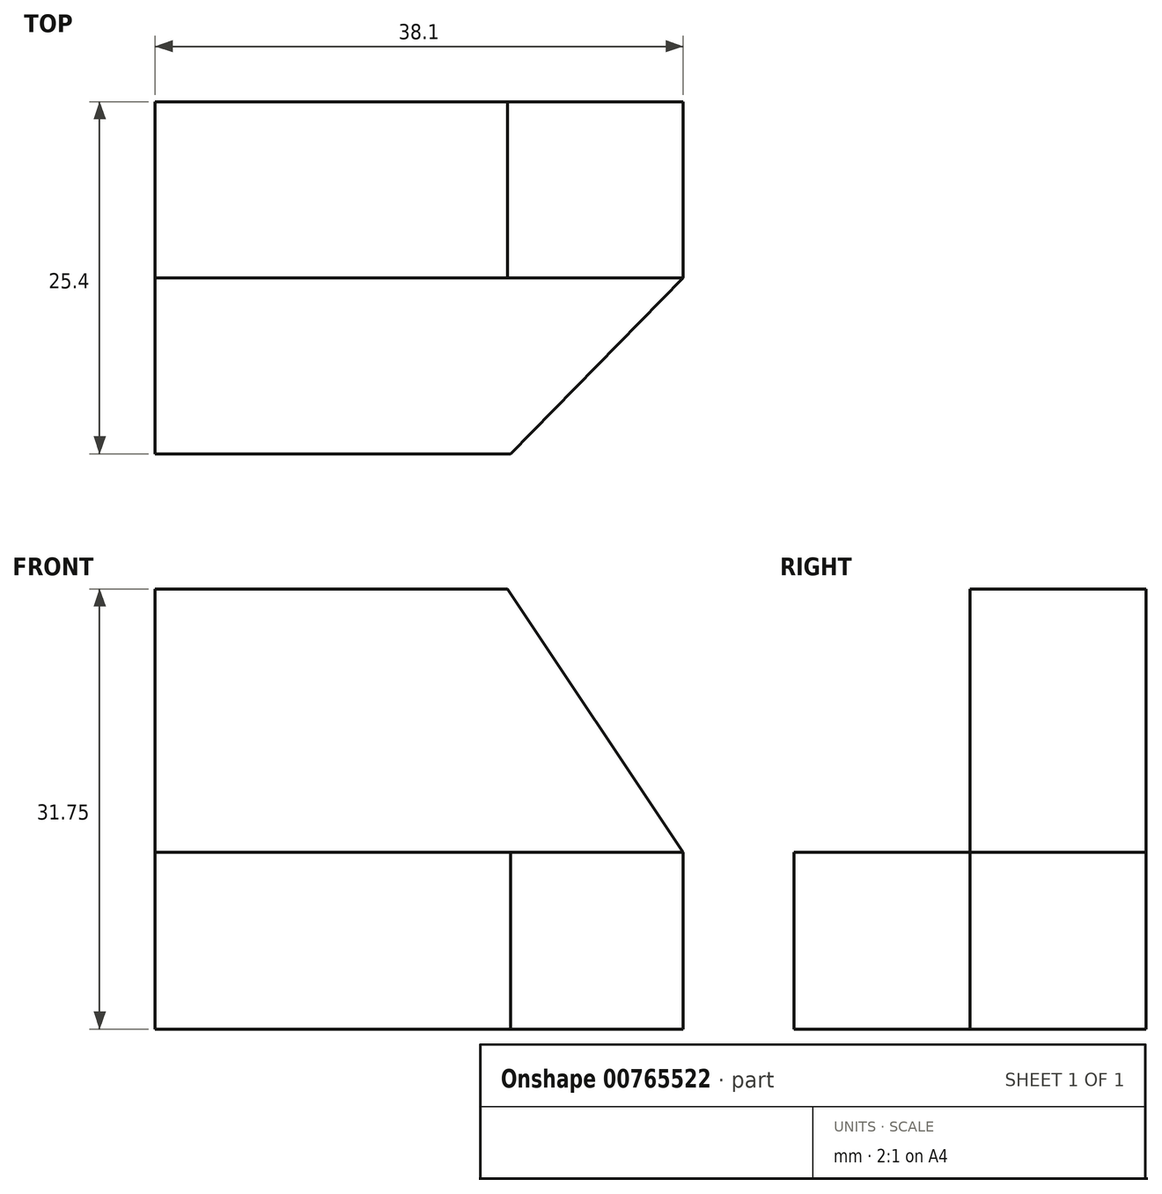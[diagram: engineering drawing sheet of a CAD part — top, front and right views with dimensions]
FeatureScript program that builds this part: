
annotation { "Feature Type Name" : "Feature", "Feature Type Description" : "" }
export const myFeature = defineFeature(function(context is Context, id is Id, definition is map)
    precondition{}
    {
        {
            var Q0;
            Q0=qCreatedBy(makeId("Front.planeOp"),FACE);
            var sketch = newSketch(context, id + "F0", { "sketchPlane" : qUnion([Q0])});
            skLineSegment(sketch, "E0", {"start": v(0, 31.75) * mm, "end": v(0, 0) * mm});
            skLineSegment(sketch, "E1", {"start": v(0, 0) * mm, "end": v(38.1, 0) * mm});
            skLineSegment(sketch, "E2", {"start": v(38.1, 0) * mm, "end": v(38.1, 31.75) * mm});
            skLineSegment(sketch, "E3", {"start": v(38.1, 31.75) * mm, "end": v(0, 31.75) * mm});
            skSolve(sketch);
        }
        {
            var Q0;
            Q0=makeQuery(id+"F0.imprint","IMPRINT",FACE,{"disambiguationData":[TD([[makeQuery(id+"F0.imprint","IMPRINT",EDGE,{"derivedFrom":sQuery(id+"F0.wireOp",EDGE,"E0")}),1.0]])]});
            extrude(context, id + "F1", {"entities" : qUnion([Q0]), "depth" : 25.4 * mm, "offsetDistance" : 25.4 * mm});
        }
        {
            var Q0;
            Q0=makeQuery(id+"F1.opExtrude","CAP_FACE",FACE,{"disambiguationData":[OSD([sQuery(id+"F0.wireOp",EDGE,"E0"),sQuery(id+"F0.wireOp",EDGE,"E1"),sQuery(id+"F0.wireOp",EDGE,"E2"),sQuery(id+"F0.wireOp",EDGE,"E3")])],"isStart":false});
            var sketch = newSketch(context, id + "F2", { "sketchPlane" : qUnion([Q0])});
            skLineSegment(sketch, "E4", {"start": v(38.1, 0) * mm, "end": v(38.1, 12.77) * mm});
            skLineSegment(sketch, "E5", {"start": v(0, 31.75) * mm, "end": v(25.43, 31.75) * mm});
            skLineSegment(sketch, "E6", {"start": v(25.43, 31.75) * mm, "end": v(38.1, 12.77) * mm});
            skSolve(sketch);
        }
        {
            var Q0;
            {var subQ0=sQuery(id+"F2.wireOp",EDGE,"E6");Q0=makeQuery(id+"F2.imprint","IMPRINT",FACE,{"disambiguationData":[TD([[makeQuery(id+"F2.imprint","IMPRINT",EDGE,{"derivedFrom":subQ0}),1.0]])]});}
            extrude(context, id + "F3", {"entities" : qUnion([Q0]), "operationType" : NewBodyOperationType.REMOVE, "endBound" : BoundingType.THROUGH_ALL, "oppositeDirection" : true, "depth" : 25.4 * mm, "offsetDistance" : 25.4 * mm});
        }
        {
            var Q0;
            Q0=makeQuery(id+"F1.opExtrude","CAP_FACE",FACE,{"disambiguationData":[OSD([sQuery(id+"F0.wireOp",EDGE,"E0"),sQuery(id+"F0.wireOp",EDGE,"E1"),sQuery(id+"F0.wireOp",EDGE,"E2"),sQuery(id+"F0.wireOp",EDGE,"E3")])],"isStart":false});
            var sketch = newSketch(context, id + "F4", { "sketchPlane" : qUnion([Q0])});
            skLineSegment(sketch, "E7", {"start": v(38.1, 12.77) * mm, "end": v(0, 12.77) * mm});
            skPoint(sketch, "E7.endSnap0", {"position": v(0, 15.88) * mm});
            skSolve(sketch);
        }
        {
            var Q0;
            {var subQ0=sQuery(id+"F4.wireOp",EDGE,"E7");Q0=makeQuery(id+"F4.imprint","IMPRINT",FACE,{"disambiguationData":[TD([[makeQuery(id+"F4.imprint","IMPRINT",EDGE,{"derivedFrom":subQ0}),-1.0]])]});}
            extrude(context, id + "F5", {"entities" : qUnion([Q0]), "operationType" : NewBodyOperationType.REMOVE, "oppositeDirection" : true, "depth" : 12.7 * mm, "offsetDistance" : 25.4 * mm});
        }
        {
            var Q0;
            Q0=makeQuery(id+"F5.boolean.opBoolean","COPY",FACE,{"derivedFrom":makeQuery(id+"F5.opExtrude","SWEPT_FACE",FACE,{"disambiguationData":[OSD([sQuery(id+"F4.wireOp",EDGE,"E7")])]})});
            var sketch = newSketch(context, id + "F6", { "sketchPlane" : qUnion([Q0])});
            skLineSegment(sketch, "E8", {"start": v(0, -25.4) * mm, "end": v(25.63, -25.4) * mm});
            skLineSegment(sketch, "E9", {"start": v(25.63, -25.4) * mm, "end": v(38.1, -12.7) * mm});
            skSolve(sketch);
        }
        {
            var Q0;
            Q0 = qSketchRegion(id + "F6", true);
            var Q1;
            {var subQ0=sQuery(id+"F6.wireOp",EDGE,"E9");Q1=makeQuery(id+"F6.imprint","IMPRINT",FACE,{"disambiguationData":[TD([[makeQuery(id+"F6.imprint","IMPRINT",EDGE,{"derivedFrom":subQ0}),-1.0]])]});}
            extrude(context, id + "F7", {"entities" : qUnion([Q0, Q1]), "operationType" : NewBodyOperationType.REMOVE, "endBound" : BoundingType.THROUGH_ALL, "oppositeDirection" : true, "depth" : 25.4 * mm, "offsetDistance" : 25.4 * mm});
        }
    });
